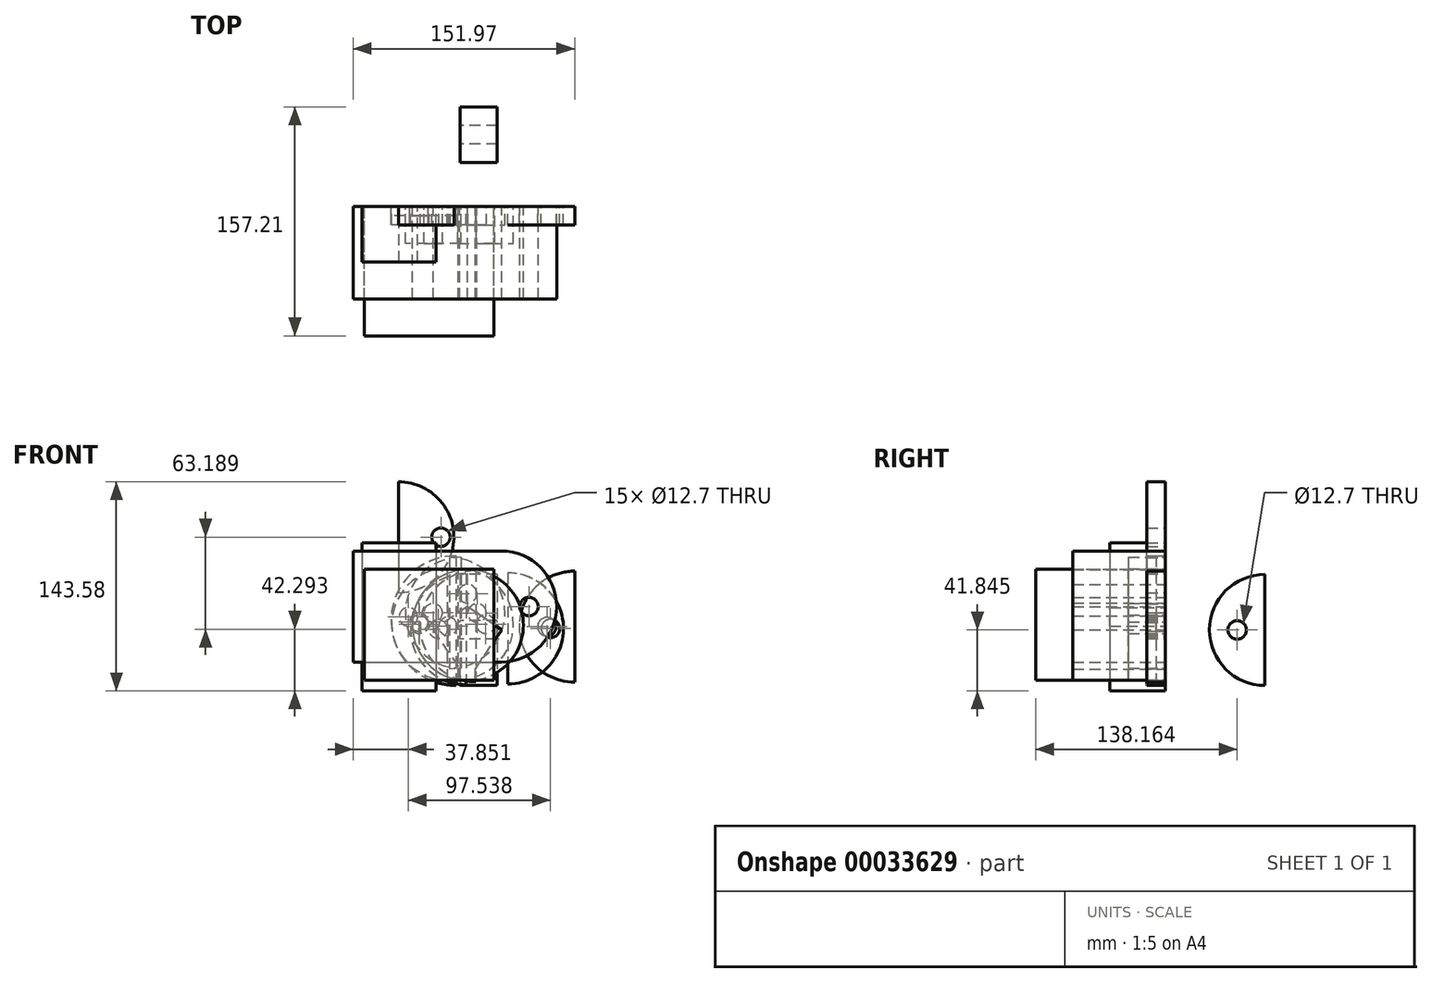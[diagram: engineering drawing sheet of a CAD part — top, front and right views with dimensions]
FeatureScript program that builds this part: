
annotation { "Feature Type Name" : "Feature", "Feature Type Description" : "" }
export const myFeature = defineFeature(function(context is Context, id is Id, definition is map)
    precondition{}
    {
        {
            var Q0;
            Q0=qCreatedBy(makeId("Front.planeOp"),FACE);
            var sketch = newSketch(context, id + "F0", { "sketchPlane" : qUnion([Q0])});
            skLineSegment(sketch, "E0.bottom", {"start": v(-67.33, 61.27) * mm, "end": v(-16.53, 61.27) * mm});
            skLineSegment(sketch, "E0.top", {"start": v(-67.33, -40.33) * mm, "end": v(-16.53, -40.33) * mm});
            skLineSegment(sketch, "E0.left", {"start": v(-67.33, 61.27) * mm, "end": v(-67.33, -40.33) * mm});
            skLineSegment(sketch, "E0.right", {"start": v(-16.53, 61.27) * mm, "end": v(-16.53, -40.33) * mm});
            skPoint(sketch, "E1", {"position": v(-16.53, 10.47) * mm});
            skCircle(sketch, "E2", {"center": v(-35.58, 10.47) * mm, "radius": 6.35 * mm});
            skSolve(sketch);
        }
        {
            var Q0;
            Q0=makeQuery(id+"F0.imprint","IMPRINT",FACE,{"disambiguationData":[TD([[makeQuery(id+"F0.imprint","IMPRINT",EDGE,{"derivedFrom":sQuery(id+"F0.wireOp",EDGE,"E0.bottom")}),-1.0]])]});
            extrude(context, id + "F1", {"entities" : qUnion([Q0]), "depth" : 38.1 * mm});
        }
        {
            var Q0;
            Q0=qCreatedBy(makeId("Front.planeOp"),FACE);
            var sketch = newSketch(context, id + "F2", { "sketchPlane" : qUnion([Q0])});
            skLineSegment(sketch, "E3.bottom", {"start": v(-73.43, 55.6) * mm, "end": v(28.17, 55.6) * mm});
            skLineSegment(sketch, "E3.top", {"start": v(-73.43, -20.6) * mm, "end": v(28.17, -20.6) * mm});
            skLineSegment(sketch, "E3.left", {"start": v(-73.43, 55.6) * mm, "end": v(-73.43, -20.6) * mm});
            skLineSegment(sketch, "E3.right", {"start": v(28.17, 55.6) * mm, "end": v(28.17, -20.6) * mm});
            skCircle(sketch, "E4", {"center": v(28.17, 17.5) * mm, "radius": 38.1 * mm});
            skCircle(sketch, "E5", {"center": v(47.22, 17.5) * mm, "radius": 6.35 * mm});
            skSolve(sketch);
        }
        {
            var Q0;
            {var subQ3=sQuery(id+"F2.wireOp",EDGE,"E3.bottom");Q0=makeQuery(id+"F2.imprint","IMPRINT",FACE,{"disambiguationData":[TD([[makeQuery(id+"F2.imprint","IMPRINT",EDGE,{"derivedFrom":subQ3}),-1.0]])]});}
            var Q1;
            {var subQ0=sQuery(id+"F2.wireOp",EDGE,"c10aab27-95d6-48ac-873c-3ab2b1cbdb17");Q1=makeQuery(id+"F2.imprint","IMPRINT",FACE,{"disambiguationData":[TD([[makeQuery(id+"F2.imprint","IMPRINT",EDGE,{"derivedFrom":subQ0}),-1.0]])]});}
            var Q2;
            {var subQ1=sQuery(id+"F2.wireOp",EDGE,"E3.right");var subQ4=makeQuery(id+"F2.imprint","INTERSECT",VERTEX,{"derivedFrom":[subQ1,sQuery(id+"F2.wireOp",EDGE,"E5")]});Q2=makeQuery(id+"F2.imprint","IMPRINT",FACE,{"disambiguationData":[TD([[makeQuery(id+"F2.imprint","IMPRINT",EDGE,{"disambiguationData":[TD([[subQ4,1.0]])],"derivedFrom":subQ1}),-1.0]])]});}
            var Q3;
            {var subQ1=sQuery(id+"F2.wireOp",EDGE,"E3.left");var subQ4=makeQuery(id+"F2.imprint","INTERSECT",VERTEX,{"derivedFrom":[subQ1,sQuery(id+"F2.wireOp",EDGE,"c10aab27-95d6-48ac-873c-3ab2b1cbdb17")]});Q3=makeQuery(id+"F2.imprint","IMPRINT",FACE,{"disambiguationData":[TD([[makeQuery(id+"F2.imprint","IMPRINT",EDGE,{"disambiguationData":[TD([[subQ4,1.0]])],"derivedFrom":subQ1}),1.0]])]});}
            var Q4;
            {var subQ0=sQuery(id+"F2.wireOp",EDGE,"E5");Q4=makeQuery(id+"F2.imprint","IMPRINT",FACE,{"disambiguationData":[TD([[makeQuery(id+"F2.imprint","IMPRINT",EDGE,{"derivedFrom":subQ0}),-1.0]])]});}
            extrude(context, id + "F3", {"entities" : qUnion([Q0, Q1, Q2, Q3, Q4]), "depth" : 63.5 * mm});
        }
        {
            var Q0;
            Q0=qCreatedBy(makeId("Front.planeOp"),FACE);
            var sketch = newSketch(context, id + "F4", { "sketchPlane" : qUnion([Q0])});
            skLineSegment(sketch, "E6.bottom", {"start": v(-65.77, 43.18) * mm, "end": v(23.13, 43.18) * mm});
            skLineSegment(sketch, "E6.top", {"start": v(-65.77, -33.02) * mm, "end": v(23.13, -33.02) * mm});
            skLineSegment(sketch, "E6.left", {"start": v(-65.77, 43.18) * mm, "end": v(-65.77, -33.02) * mm});
            skLineSegment(sketch, "E6.right", {"start": v(23.13, 43.18) * mm, "end": v(23.13, -33.02) * mm});
            skSolve(sketch);
        }
        {
            var Q0;
            {var subQ0=sQuery(id+"F4.wireOp",EDGE,"3719a03e-5642-422c-adcf-e18c0188a4ef");Q0=makeQuery(id+"F4.imprint","IMPRINT",FACE,{"disambiguationData":[TD([[makeQuery(id+"F4.imprint","IMPRINT",EDGE,{"derivedFrom":subQ0}),-1.0]])]});}
            var Q1;
            {var subQ1=sQuery(id+"F4.wireOp",EDGE,"E6.left");var subQ4=makeQuery(id+"F4.imprint","INTERSECT",VERTEX,{"derivedFrom":[subQ1,sQuery(id+"F4.wireOp",EDGE,"3719a03e-5642-422c-adcf-e18c0188a4ef")]});Q1=makeQuery(id+"F4.imprint","IMPRINT",FACE,{"disambiguationData":[TD([[makeQuery(id+"F4.imprint","IMPRINT",EDGE,{"disambiguationData":[TD([[subQ4,1.0]])],"derivedFrom":subQ1}),1.0]])]});}
            var Q2;
            {var subQ3=sQuery(id+"F4.wireOp",EDGE,"E6.bottom");Q2=makeQuery(id+"F4.imprint","IMPRINT",FACE,{"disambiguationData":[TD([[makeQuery(id+"F4.imprint","IMPRINT",EDGE,{"derivedFrom":subQ3}),-1.0]])]});}
            var Q3;
            {var subQ1=sQuery(id+"F4.wireOp",EDGE,"E6.right");var subQ4=makeQuery(id+"F4.imprint","INTERSECT",VERTEX,{"derivedFrom":[subQ1,sQuery(id+"F4.wireOp",EDGE,"62eb02e2-4036-406e-8970-44f0c3233555")]});Q3=makeQuery(id+"F4.imprint","IMPRINT",FACE,{"disambiguationData":[TD([[makeQuery(id+"F4.imprint","IMPRINT",EDGE,{"disambiguationData":[TD([[subQ4,1.0]])],"derivedFrom":subQ1}),-1.0]])]});}
            var Q4;
            {var subQ0=sQuery(id+"F4.wireOp",EDGE,"62eb02e2-4036-406e-8970-44f0c3233555");Q4=makeQuery(id+"F4.imprint","IMPRINT",FACE,{"disambiguationData":[TD([[makeQuery(id+"F4.imprint","IMPRINT",EDGE,{"derivedFrom":subQ0}),-1.0]])]});}
            extrude(context, id + "F5", {"entities" : qUnion([Q0, Q1, Q2, Q3, Q4]), "depth" : 88.9 * mm});
        }
        {
            var Q0;
            Q0=qCreatedBy(makeId("Front.planeOp"),FACE);
            var sketch = newSketch(context, id + "F6", { "sketchPlane" : qUnion([Q0])});
            skCircle(sketch, "E7", {"center": v(78.54, 3.74) * mm, "radius": 38.1 * mm});
            skCircle(sketch, "E8", {"center": v(59.49, 3.74) * mm, "radius": 6.35 * mm});
            skLineSegment(sketch, "E9", {"start": v(78.54, 41.84) * mm, "end": v(78.54, -34.36) * mm});
            skSolve(sketch);
        }
        {
            var Q0;
            Q0=qCreatedBy(makeId("Front.planeOp"),FACE);
            var sketch = newSketch(context, id + "F7", { "sketchPlane" : qUnion([Q0])});
            skCircle(sketch, "E10", {"center": v(-2.98, 7.92) * mm, "radius": 44.45 * mm});
            skCircle(sketch, "E11", {"center": v(-28.35, 6.86) * mm, "radius": 6.35 * mm});
            skLineSegment(sketch, "E12", {"start": v(-2.98, 52.37) * mm, "end": v(-2.98, -36.53) * mm});
            skSolve(sketch);
        }
        {
            var Q0;
            Q0=makeQuery(id+"F7.imprint","IMPRINT",FACE,{"disambiguationData":[TD([[makeQuery(id+"F7.imprint","IMPRINT",EDGE,{"derivedFrom":sQuery(id+"F7.wireOp",EDGE,"E11")}),-1.0]])]});
            extrude(context, id + "F8", {"entities" : qUnion([Q0]), "depth" : 6.35 * mm});
        }
        {
            var Q0;
            Q0=qCreatedBy(makeId("Front.planeOp"),FACE);
            var sketch = newSketch(context, id + "F9", { "sketchPlane" : qUnion([Q0])});
            skCircle(sketch, "E13", {"center": v(5.27, 4.74) * mm, "radius": 38.1 * mm});
            skLineSegment(sketch, "E14", {"start": v(5.04, 17.44) * mm, "end": v(-18.5, 1.52) * mm});
            skLineSegment(sketch, "E15", {"start": v(-18.5, 1.52) * mm, "end": v(-0.29, -25.4) * mm});
            skLineSegment(sketch, "E16", {"start": v(0.17, -33.02) * mm, "end": v(10.37, -33.02) * mm});
            skLineSegment(sketch, "E17", {"start": v(10.37, -33.02) * mm, "end": v(10.37, -25.4) * mm});
            skLineSegment(sketch, "E18", {"start": v(10.37, -25.4) * mm, "end": v(28.57, 1.52) * mm});
            skLineSegment(sketch, "E19", {"start": v(28.57, 1.52) * mm, "end": v(5.04, 17.44) * mm});
            skLineSegment(sketch, "E20", {"start": v(-0.29, -25.4) * mm, "end": v(-0.29, -33.02) * mm});
            skPoint(sketch, "E20.endSnap0", {"position": v(5.27, -33.02) * mm});
            skCircle(sketch, "E21", {"center": v(5.04, 26.33) * mm, "radius": 6.35 * mm});
            skSolve(sketch);
        }
        {
            var Q0;
            Q0=makeQuery(id+"F9.imprint","IMPRINT",FACE,{"disambiguationData":[TD([[makeQuery(id+"F9.imprint","IMPRINT",EDGE,{"derivedFrom":sQuery(id+"F9.wireOp",EDGE,"E14")}),-1.0]])]});
            extrude(context, id + "F10", {"entities" : qUnion([Q0]), "depth" : 63.5 * mm});
        }
        {
            var Q0;
            Q0=qCreatedBy(makeId("Front.planeOp"),FACE);
            var sketch = newSketch(context, id + "F11", { "sketchPlane" : qUnion([Q0])});
            skCircle(sketch, "E22", {"center": v(4.04, 1.96) * mm, "radius": 38.1 * mm});
            skLineSegment(sketch, "E23", {"start": v(4.04, 40.06) * mm, "end": v(4.04, -36.14) * mm});
            skCircle(sketch, "E24", {"center": v(-15, 1.96) * mm, "radius": 6.35 * mm});
            skSolve(sketch);
        }
        {
            var Q0;
            {var subQ0=sQuery(id+"F11.wireOp",EDGE,"E23");Q0=makeQuery(id+"F11.imprint","IMPRINT",FACE,{"disambiguationData":[TD([[makeQuery(id+"F11.imprint","IMPRINT",EDGE,{"derivedFrom":subQ0}),-1.0]])]});}
            extrude(context, id + "F12", {"entities" : qUnion([Q0]), "depth" : 12.7 * mm});
        }
        {
            var Q0;
            Q0=qCreatedBy(makeId("Front.planeOp"),FACE);
            var sketch = newSketch(context, id + "F13", { "sketchPlane" : qUnion([Q0])});
            skCircle(sketch, "E25", {"center": v(0.46, 13.28) * mm, "radius": 38.1 * mm});
            skLineSegment(sketch, "E26", {"start": v(0.46, 51.38) * mm, "end": v(0.46, -24.82) * mm});
            skCircle(sketch, "E27", {"center": v(-18.59, 13.28) * mm, "radius": 6.35 * mm});
            skSolve(sketch);
        }
        {
            var Q0;
            Q0=makeQuery(id+"F13.imprint","IMPRINT",FACE,{"disambiguationData":[TD([[makeQuery(id+"F13.imprint","IMPRINT",EDGE,{"derivedFrom":sQuery(id+"F13.wireOp",EDGE,"e17e4a17-17db-4a1e-885f-7355e2b7c3f0")}),-1.0]])]});
            var Q1;
            {var subQ0=sQuery(id+"F13.wireOp",EDGE,"E26");Q1=makeQuery(id+"F13.imprint","IMPRINT",FACE,{"disambiguationData":[TD([[makeQuery(id+"F13.imprint","IMPRINT",EDGE,{"derivedFrom":subQ0}),-1.0]])]});}
            extrude(context, id + "F14", {"entities" : qUnion([Q0, Q1]), "depth" : 12.7 * mm});
        }
        {
            var Q0;
            Q0=makeQuery(id+"F6.imprint","IMPRINT",FACE,{"disambiguationData":[TD([[makeQuery(id+"F6.imprint","IMPRINT",EDGE,{"derivedFrom":sQuery(id+"F6.wireOp",EDGE,"E8")}),-1.0]])]});
            extrude(context, id + "F15", {"entities" : qUnion([Q0]), "depth" : 12.7 * mm});
        }
        {
            var Q0;
            Q0=makeQuery(id+"F7.imprint","IMPRINT",FACE,{"disambiguationData":[TD([[makeQuery(id+"F7.imprint","IMPRINT",EDGE,{"derivedFrom":sQuery(id+"F7.wireOp",EDGE,"E11")}),-1.0]])]});
            extrude(context, id + "F16", {"entities" : qUnion([Q0]), "depth" : 12.7 * mm});
        }
        {
            var Q0;
            Q0=qCreatedBy(makeId("Front.planeOp"),FACE);
            var sketch = newSketch(context, id + "F17", { "sketchPlane" : qUnion([Q0])});
            skCircle(sketch, "E28", {"center": v(32.75, 2.5) * mm, "radius": 38.1 * mm});
            skCircle(sketch, "E29", {"center": v(61.96, 2.5) * mm, "radius": 6.35 * mm});
            skLineSegment(sketch, "E30", {"start": v(32.75, 40.6) * mm, "end": v(32.75, -35.6) * mm});
            skSolve(sketch);
        }
        {
            var Q0;
            Q0=makeQuery(id+"F17.imprint","IMPRINT",FACE,{"disambiguationData":[TD([[makeQuery(id+"F17.imprint","IMPRINT",EDGE,{"derivedFrom":sQuery(id+"F17.wireOp",EDGE,"E29")}),-1.0]])]});
            extrude(context, id + "F18", {"entities" : qUnion([Q0]), "depth" : 12.7 * mm});
        }
        {
            var Q0;
            Q0=qCreatedBy(makeId("Front.planeOp"),FACE);
            var sketch = newSketch(context, id + "F19", { "sketchPlane" : qUnion([Q0])});
            skCircle(sketch, "E31", {"center": v(-42.42, 65.15) * mm, "radius": 38.1 * mm});
            skCircle(sketch, "E32", {"center": v(-13.21, 65.15) * mm, "radius": 6.35 * mm});
            skLineSegment(sketch, "E33", {"start": v(-42.42, 103.25) * mm, "end": v(-42.42, 27.05) * mm});
            skSolve(sketch);
        }
        {
            var Q0;
            Q0=makeQuery(id+"F19.imprint","IMPRINT",FACE,{"disambiguationData":[TD([[makeQuery(id+"F19.imprint","IMPRINT",EDGE,{"derivedFrom":sQuery(id+"F19.wireOp",EDGE,"E32")}),-1.0]])]});
            extrude(context, id + "F20", {"entities" : qUnion([Q0]), "depth" : 12.7 * mm});
        }
        {
            var Q0;
            {var subQ0=sQuery(id+"F13.wireOp",EDGE,"E26");Q0=makeQuery(id+"F13.imprint","IMPRINT",FACE,{"disambiguationData":[TD([[makeQuery(id+"F13.imprint","IMPRINT",EDGE,{"derivedFrom":subQ0}),-1.0]])]});}
            extrude(context, id + "F21", {"entities" : qUnion([Q0]), "depth" : 25.4 * mm});
        }
        {
            var Q0;
            Q0=qCreatedBy(makeId("Front.planeOp"),FACE);
            var sketch = newSketch(context, id + "F22", { "sketchPlane" : qUnion([Q0])});
            skCircle(sketch, "E34", {"center": v(-7.39, 13.05) * mm, "radius": 38.1 * mm});
            skCircle(sketch, "E35", {"center": v(11.66, 13.05) * mm, "radius": 6.35 * mm});
            skLineSegment(sketch, "E36", {"start": v(-7.39, 51.15) * mm, "end": v(-7.39, -25.05) * mm});
            skSolve(sketch);
        }
        {
            var Q0;
            Q0=makeQuery(id+"F22.imprint","IMPRINT",FACE,{"disambiguationData":[TD([[makeQuery(id+"F22.imprint","IMPRINT",EDGE,{"derivedFrom":sQuery(id+"F22.wireOp",EDGE,"E35")}),-1.0]])]});
            extrude(context, id + "F23", {"entities" : qUnion([Q0]), "depth" : 12.7 * mm});
        }
        {
            var Q0;
            Q0=qCreatedBy(makeId("Right.planeOp"),FACE);
            var sketch = newSketch(context, id + "F24", { "sketchPlane" : qUnion([Q0])});
            skCircle(sketch, "E37", {"center": v(68.31, 1.52) * mm, "radius": 38.1 * mm});
            skCircle(sketch, "E38", {"center": v(49.26, 1.52) * mm, "radius": 6.35 * mm});
            skLineSegment(sketch, "E39", {"start": v(68.31, 39.62) * mm, "end": v(68.31, -36.58) * mm});
            skSolve(sketch);
        }
        {
            var Q0;
            Q0=makeQuery(id+"F24.imprint","IMPRINT",FACE,{"disambiguationData":[TD([[makeQuery(id+"F24.imprint","IMPRINT",EDGE,{"derivedFrom":sQuery(id+"F24.wireOp",EDGE,"E38")}),-1.0]])]});
            extrude(context, id + "F25", {"entities" : qUnion([Q0]), "depth" : 25.4 * mm});
        }
        {
            var Q0;
            Q0=qCreatedBy(makeId("Front.planeOp"),FACE);
            var sketch = newSketch(context, id + "F26", { "sketchPlane" : qUnion([Q0])});
            skCircle(sketch, "E40", {"center": v(-1.62, 5.43) * mm, "radius": 38.1 * mm});
            skCircle(sketch, "E41", {"center": v(17.43, 5.43) * mm, "radius": 6.35 * mm});
            skLineSegment(sketch, "E42", {"start": v(-1.62, 43.53) * mm, "end": v(-1.62, -32.67) * mm});
            skSolve(sketch);
        }
        {
            var Q0;
            Q0=makeQuery(id+"F26.imprint","IMPRINT",FACE,{"disambiguationData":[TD([[makeQuery(id+"F26.imprint","IMPRINT",EDGE,{"derivedFrom":sQuery(id+"F26.wireOp",EDGE,"E41")}),-1.0]])]});
            extrude(context, id + "F27", {"entities" : qUnion([Q0]), "depth" : 25.4 * mm});
        }
        {
            var Q0;
            Q0=qCreatedBy(makeId("Front.planeOp"),FACE);
            var sketch = newSketch(context, id + "F28", { "sketchPlane" : qUnion([Q0])});
            skCircle(sketch, "E43", {"center": v(-8.91, 5.4) * mm, "radius": 38.1 * mm});
            skCircle(sketch, "E44", {"center": v(-27.96, 5.4) * mm, "radius": 6.35 * mm});
            skLineSegment(sketch, "E45", {"start": v(-8.91, 43.5) * mm, "end": v(-8.91, -32.7) * mm});
            skSolve(sketch);
        }
        {
            var Q0;
            Q0=makeQuery(id+"F28.imprint","IMPRINT",FACE,{"disambiguationData":[TD([[makeQuery(id+"F28.imprint","IMPRINT",EDGE,{"derivedFrom":sQuery(id+"F28.wireOp",EDGE,"E44")}),-1.0]])]});
            extrude(context, id + "F29", {"entities" : qUnion([Q0]), "depth" : 12.7 * mm});
        }
        {
            var Q0;
            Q0=qCreatedBy(makeId("Front.planeOp"),FACE);
            var sketch = newSketch(context, id + "F30", { "sketchPlane" : qUnion([Q0])});
            skCircle(sketch, "E46", {"center": v(10.67, 4) * mm, "radius": 38.1 * mm});
            skCircle(sketch, "E47", {"center": v(-8.38, 4) * mm, "radius": 6.35 * mm});
            skLineSegment(sketch, "E48", {"start": v(10.67, 42.1) * mm, "end": v(10.67, -34.1) * mm});
            skSolve(sketch);
        }
        {
            var Q0;
            Q0=makeQuery(id+"F30.imprint","IMPRINT",FACE,{"disambiguationData":[TD([[makeQuery(id+"F30.imprint","IMPRINT",EDGE,{"derivedFrom":sQuery(id+"F30.wireOp",EDGE,"E47")}),-1.0]])]});
            extrude(context, id + "F31", {"entities" : qUnion([Q0]), "depth" : 12.7 * mm});
        }
    });
